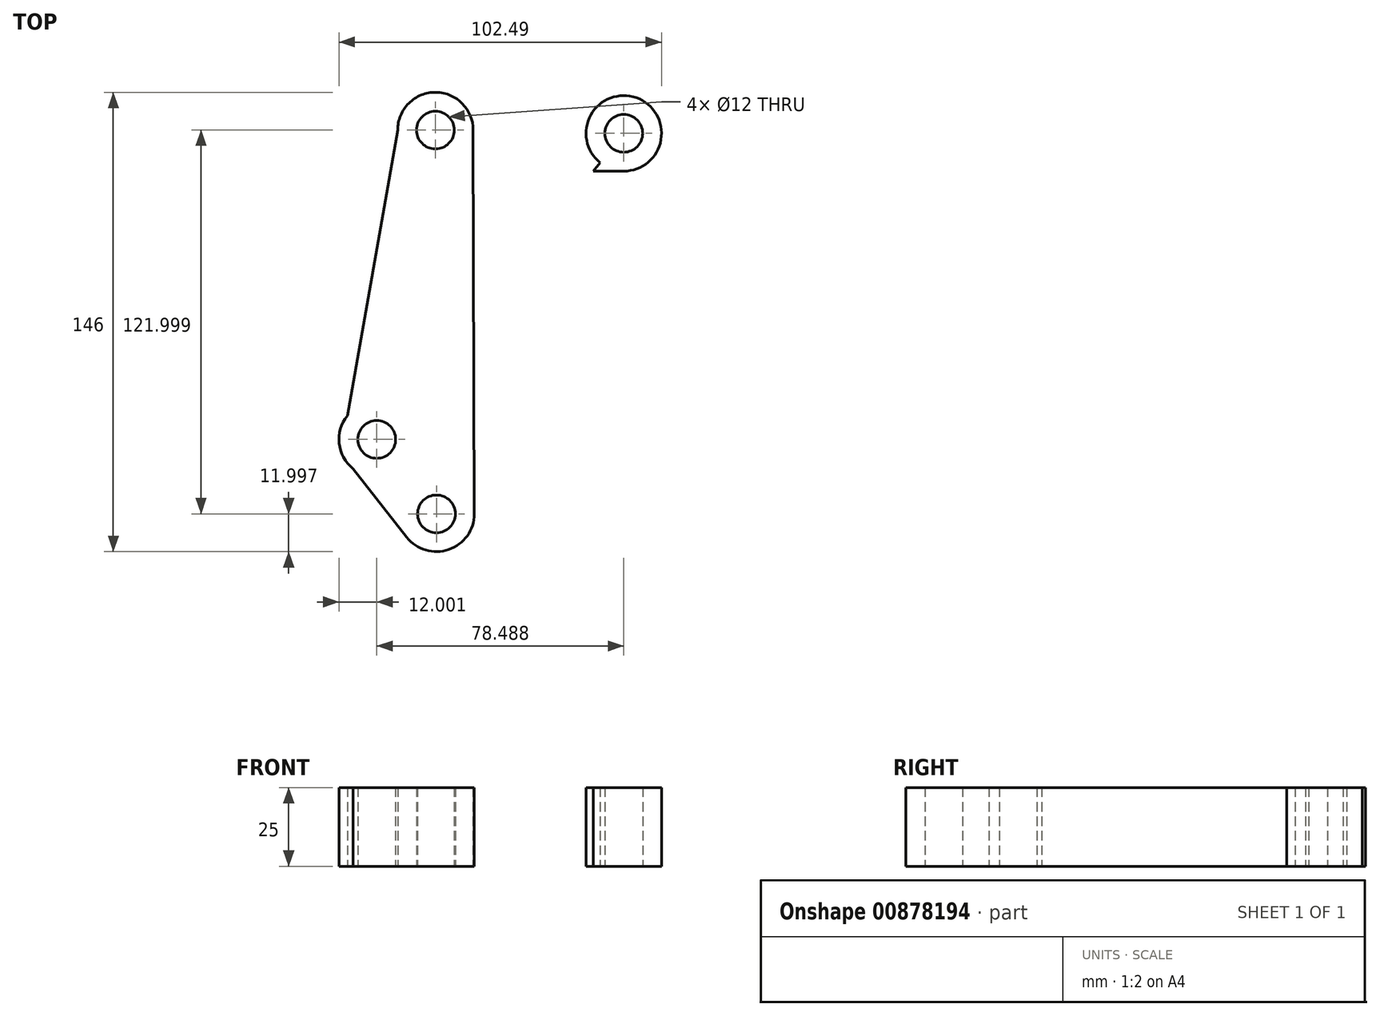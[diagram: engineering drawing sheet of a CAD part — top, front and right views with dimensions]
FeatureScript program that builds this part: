
annotation { "Feature Type Name" : "Feature", "Feature Type Description" : "" }
export const myFeature = defineFeature(function(context is Context, id is Id, definition is map)
    precondition{}
    {
        {
            var Q0;
            Q0=qCreatedBy(makeId("Top.planeOp"),FACE);
            var sketch = newSketch(context, id + "F0", { "sketchPlane" : qUnion([Q0])});
            skCircle(sketch, "E0", {"center": v(0, 0) * mm, "radius": 162 * mm, "construction": true});
            skLineSegment(sketch, "E1", {"start": v(-162, 0) * mm, "end": v(-116, 0) * mm, "construction": true});
            skLineSegment(sketch, "E2", {"start": v(-116, 0) * mm, "end": v(-70, 0) * mm, "construction": true});
            skCircle(sketch, "E3", {"center": v(0, 0) * mm, "radius": 65 * mm, "construction": true});
            skCircle(sketch, "E4", {"center": v(25.35, 59.85) * mm, "radius": 6 * mm});
            skCircle(sketch, "E5", {"center": v(-53.14, -37.43) * mm, "radius": 6 * mm});
            skLineSegment(sketch, "E6.trimOffspring", {"start": v(-22.45, 61) * mm, "end": v(-22.34, 61) * mm});
            skArc(sketch, "E7.trimOffspring", {"start": v(-22.34, 61) * mm, "mid": v(-22.34, 61.02) * mm, "end": v(-22.34, 61.04) * mm});
            skCircle(sketch, "E8", {"center": v(0, 0) * mm, "radius": 70 * mm, "construction": true});
            skLineSegment(sketch, "E9", {"start": v(25.35, 59.85) * mm, "end": v(-53.14, -37.43) * mm});
            skCircle(sketch, "E10", {"center": v(-34.5, 60.9) * mm, "radius": 6 * mm});
            skCircle(sketch, "E11", {"center": v(-34.17, -61.1) * mm, "radius": 6 * mm});
            skLineSegment(sketch, "E12", {"start": v(-34.5, 60.9) * mm, "end": v(-34.17, -61.1) * mm});
            skCircle(sketch, "E13", {"center": v(-53.14, -37.43) * mm, "radius": 12 * mm});
            skCircle(sketch, "E14", {"center": v(-34.17, -61.1) * mm, "radius": 12 * mm});
            skCircle(sketch, "E15", {"center": v(-34.5, 60.9) * mm, "radius": 12 * mm});
            skCircle(sketch, "E16", {"center": v(25.35, 59.85) * mm, "radius": 12 * mm});
            skLineSegment(sketch, "E17", {"start": v(-34.5, 60.9) * mm, "end": v(-22.5, 60.9) * mm});
            skLineSegment(sketch, "E18", {"start": v(-34.5, 60.9) * mm, "end": v(-46.5, 60.87) * mm});
            skLineSegment(sketch, "E19", {"start": v(-53.14, -37.43) * mm, "end": v(-62.48, -29.9) * mm});
            skLineSegment(sketch, "E20", {"start": v(-62.48, -29.9) * mm, "end": v(-46.5, 60.87) * mm});
            skLineSegment(sketch, "E21", {"start": v(-53.14, -37.43) * mm, "end": v(-60.67, -46.77) * mm});
            skLineSegment(sketch, "E22", {"start": v(-34.17, -61.1) * mm, "end": v(-34.17, -73.1) * mm});
            skLineSegment(sketch, "E23", {"start": v(-60.67, -46.77) * mm, "end": v(-43.6, -68.5) * mm});
            skLineSegment(sketch, "E24", {"start": v(-34.17, -61.1) * mm, "end": v(-22.17, -61.1) * mm});
            skLineSegment(sketch, "E25", {"start": v(-22.17, -61.1) * mm, "end": v(-22.5, 60.9) * mm});
            skLineSegment(sketch, "E26", {"start": v(25.35, 59.85) * mm, "end": v(25.35, 47.85) * mm});
            skLineSegment(sketch, "E27", {"start": v(25.35, 47.85) * mm, "end": v(-22.47, 47.85) * mm});
            skLineSegment(sketch, "E28", {"start": v(-34.5, 60.9) * mm, "end": v(-34.33, 72.9) * mm});
            skLineSegment(sketch, "E29", {"start": v(25.35, 59.85) * mm, "end": v(25.35, 71.85) * mm});
            skLineSegment(sketch, "E30", {"start": v(-34.33, 72.9) * mm, "end": v(25.35, 71.85) * mm});
            skSolve(sketch);
        }
        {
            var Q0;
            {var subQ0=sQuery(id+"F0.wireOp",EDGE,"E27");var subQ1=sQuery(id+"F0.wireOp",EDGE,"E9");var subQ2=makeQuery(id+"F0.imprint","INTERSECT",VERTEX,{"derivedFrom":[subQ1,subQ0]});Q0=makeQuery(id+"F0.imprint","IMPRINT",FACE,{"disambiguationData":[TD([[makeQuery(id+"F0.imprint","IMPRINT",EDGE,{"disambiguationData":[TD([[subQ2,1.0]])],"derivedFrom":subQ1}),1.0]])]});}
            var Q1;
            {var subQ0=sQuery(id+"F0.wireOp",EDGE,"E29");var subQ1=sQuery(id+"F0.wireOp",EDGE,"E4");var subQ2=makeQuery(id+"F0.imprint","INTERSECT",VERTEX,{"derivedFrom":[subQ1,subQ0]});Q1=makeQuery(id+"F0.imprint","IMPRINT",FACE,{"disambiguationData":[TD([[makeQuery(id+"F0.imprint","IMPRINT",EDGE,{"disambiguationData":[TD([[subQ2,1.0]])],"derivedFrom":subQ1}),-1.0]])]});}
            var Q2;
            {var subQ0=sQuery(id+"F0.wireOp",EDGE,"E19");var subQ1=sQuery(id+"F0.wireOp",EDGE,"E5");var subQ2=makeQuery(id+"F0.imprint","INTERSECT",VERTEX,{"derivedFrom":[subQ1,subQ0]});Q2=makeQuery(id+"F0.imprint","IMPRINT",FACE,{"disambiguationData":[TD([[makeQuery(id+"F0.imprint","IMPRINT",EDGE,{"disambiguationData":[TD([[subQ2,-1.0]])],"derivedFrom":subQ1}),-1.0]])]});}
            var Q3;
            {var subQ0=sQuery(id+"F0.wireOp",EDGE,"E25");var subQ1=sQuery(id+"F0.wireOp",EDGE,"E9");var subQ2=makeQuery(id+"F0.imprint","INTERSECT",VERTEX,{"derivedFrom":[subQ1,subQ0]});Q3=makeQuery(id+"F0.imprint","IMPRINT",FACE,{"disambiguationData":[TD([[makeQuery(id+"F0.imprint","IMPRINT",EDGE,{"disambiguationData":[TD([[subQ2,-1.0]])],"derivedFrom":subQ1}),1.0]])]});}
            var Q4;
            {var subQ0=sQuery(id+"F0.wireOp",EDGE,"E28");var subQ1=sQuery(id+"F0.wireOp",EDGE,"E10");var subQ2=makeQuery(id+"F0.imprint","INTERSECT",VERTEX,{"derivedFrom":[subQ1,subQ0]});Q4=makeQuery(id+"F0.imprint","IMPRINT",FACE,{"disambiguationData":[TD([[makeQuery(id+"F0.imprint","IMPRINT",EDGE,{"disambiguationData":[TD([[subQ2,-1.0]])],"derivedFrom":subQ1}),-1.0]])]});}
            var Q5;
            {var subQ0=sQuery(id+"F0.wireOp",EDGE,"E24");var subQ1=sQuery(id+"F0.wireOp",EDGE,"E11");var subQ2=makeQuery(id+"F0.imprint","INTERSECT",VERTEX,{"derivedFrom":[subQ1,subQ0]});Q5=makeQuery(id+"F0.imprint","IMPRINT",FACE,{"disambiguationData":[TD([[makeQuery(id+"F0.imprint","IMPRINT",EDGE,{"disambiguationData":[TD([[subQ2,1.0]])],"derivedFrom":subQ1}),-1.0]])]});}
            var Q6;
            {var subQ0=sQuery(id+"F0.wireOp",EDGE,"E9");var subQ1=sQuery(id+"F0.wireOp",EDGE,"E4");var subQ2=makeQuery(id+"F0.imprint","INTERSECT",VERTEX,{"derivedFrom":[subQ1,subQ0]});Q6=makeQuery(id+"F0.imprint","IMPRINT",FACE,{"disambiguationData":[TD([[makeQuery(id+"F0.imprint","IMPRINT",EDGE,{"disambiguationData":[TD([[subQ2,1.0]])],"derivedFrom":subQ1}),-1.0]])]});}
            var Q7;
            {var subQ0=sQuery(id+"F0.wireOp",EDGE,"E9");var subQ1=sQuery(id+"F0.wireOp",EDGE,"E4");var subQ2=makeQuery(id+"F0.imprint","INTERSECT",VERTEX,{"derivedFrom":[subQ1,subQ0]});Q7=makeQuery(id+"F0.imprint","IMPRINT",FACE,{"disambiguationData":[TD([[makeQuery(id+"F0.imprint","IMPRINT",EDGE,{"disambiguationData":[TD([[subQ2,-1.0]])],"derivedFrom":subQ1}),-1.0]])]});}
            var Q8;
            {var subQ0=sQuery(id+"F0.wireOp",EDGE,"E19");var subQ1=sQuery(id+"F0.wireOp",EDGE,"E5");var subQ2=makeQuery(id+"F0.imprint","INTERSECT",VERTEX,{"derivedFrom":[subQ1,subQ0]});Q8=makeQuery(id+"F0.imprint","IMPRINT",FACE,{"disambiguationData":[TD([[makeQuery(id+"F0.imprint","IMPRINT",EDGE,{"disambiguationData":[TD([[subQ2,1.0]])],"derivedFrom":subQ1}),-1.0]])]});}
            var Q9;
            {var subQ0=sQuery(id+"F0.wireOp",EDGE,"E9");var subQ1=sQuery(id+"F0.wireOp",EDGE,"E5");var subQ2=makeQuery(id+"F0.imprint","INTERSECT",VERTEX,{"derivedFrom":[subQ1,subQ0]});Q9=makeQuery(id+"F0.imprint","IMPRINT",FACE,{"disambiguationData":[TD([[makeQuery(id+"F0.imprint","IMPRINT",EDGE,{"disambiguationData":[TD([[subQ2,1.0]])],"derivedFrom":subQ1}),-1.0]])]});}
            var Q10;
            {var subQ0=sQuery(id+"F0.wireOp",EDGE,"E20");Q10=makeQuery(id+"F0.imprint","IMPRINT",FACE,{"disambiguationData":[TD([[makeQuery(id+"F0.imprint","IMPRINT",EDGE,{"derivedFrom":subQ0}),-1.0]])]});}
            var Q11;
            {var subQ0=sQuery(id+"F0.wireOp",EDGE,"E23");Q11=makeQuery(id+"F0.imprint","IMPRINT",FACE,{"disambiguationData":[TD([[makeQuery(id+"F0.imprint","IMPRINT",EDGE,{"derivedFrom":subQ0}),1.0]])]});}
            var Q12;
            {var subQ0=sQuery(id+"F0.wireOp",EDGE,"E28");var subQ4=sQuery(id+"F0.wireOp",EDGE,"E10");var subQ5=makeQuery(id+"F0.imprint","INTERSECT",VERTEX,{"derivedFrom":[subQ4,subQ0]});Q12=makeQuery(id+"F0.imprint","IMPRINT",FACE,{"disambiguationData":[TD([[makeQuery(id+"F0.imprint","IMPRINT",EDGE,{"disambiguationData":[TD([[subQ5,1.0]])],"derivedFrom":subQ4}),-1.0]])]});}
            var Q13;
            {var subQ0=sQuery(id+"F0.wireOp",EDGE,"E18");var subQ1=sQuery(id+"F0.wireOp",EDGE,"E10");var subQ2=makeQuery(id+"F0.imprint","INTERSECT",VERTEX,{"derivedFrom":[subQ1,subQ0]});Q13=makeQuery(id+"F0.imprint","IMPRINT",FACE,{"disambiguationData":[TD([[makeQuery(id+"F0.imprint","IMPRINT",EDGE,{"disambiguationData":[TD([[subQ2,-1.0]])],"derivedFrom":subQ1}),-1.0]])]});}
            var Q14;
            {var subQ2=sQuery(id+"F0.wireOp",EDGE,"E12");var subQ6=sQuery(id+"F0.wireOp",EDGE,"E11");var subQ7=makeQuery(id+"F0.imprint","INTERSECT",VERTEX,{"derivedFrom":[subQ6,subQ2]});Q14=makeQuery(id+"F0.imprint","IMPRINT",FACE,{"disambiguationData":[TD([[makeQuery(id+"F0.imprint","IMPRINT",EDGE,{"disambiguationData":[TD([[subQ7,1.0]])],"derivedFrom":subQ6}),-1.0]])]});}
            var Q15;
            {var subQ4=sQuery(id+"F0.wireOp",EDGE,"E12");var subQ6=sQuery(id+"F0.wireOp",EDGE,"E11");var subQ7=makeQuery(id+"F0.imprint","INTERSECT",VERTEX,{"derivedFrom":[subQ6,subQ4]});Q15=makeQuery(id+"F0.imprint","IMPRINT",FACE,{"disambiguationData":[TD([[makeQuery(id+"F0.imprint","IMPRINT",EDGE,{"disambiguationData":[TD([[subQ7,-1.0]])],"derivedFrom":subQ6}),-1.0]])]});}
            var Q16;
            {var subQ5=sQuery(id+"F0.wireOp",EDGE,"E30");Q16=makeQuery(id+"F0.imprint","IMPRINT",FACE,{"disambiguationData":[TD([[makeQuery(id+"F0.imprint","IMPRINT",EDGE,{"derivedFrom":subQ5}),-1.0]])]});}
            var Q17;
            {var subQ0=sQuery(id+"F0.wireOp",EDGE,"E25");var subQ6=sQuery(id+"F0.wireOp",EDGE,"E9");var subQ7=makeQuery(id+"F0.imprint","INTERSECT",VERTEX,{"derivedFrom":[subQ6,subQ0]});Q17=makeQuery(id+"F0.imprint","IMPRINT",FACE,{"disambiguationData":[TD([[makeQuery(id+"F0.imprint","IMPRINT",EDGE,{"disambiguationData":[TD([[subQ7,-1.0]])],"derivedFrom":subQ6}),-1.0]])]});}
            var Q18;
            {var subQ0=sQuery(id+"F0.wireOp",EDGE,"E17");var subQ1=sQuery(id+"F0.wireOp",EDGE,"E10");var subQ2=makeQuery(id+"F0.imprint","INTERSECT",VERTEX,{"derivedFrom":[subQ1,subQ0]});Q18=makeQuery(id+"F0.imprint","IMPRINT",FACE,{"disambiguationData":[TD([[makeQuery(id+"F0.imprint","IMPRINT",EDGE,{"disambiguationData":[TD([[subQ2,1.0]])],"derivedFrom":subQ1}),-1.0]])]});}
            extrude(context, id + "F1", {"entities" : qUnion([Q0, Q1, Q2, Q3, Q4, Q5, Q6, Q7, Q8, Q9, Q10, Q11, Q12, Q13, Q14, Q15, Q16, Q17, Q18]), "depth" : 25 * mm, "offsetDistance" : 25 * mm});
        }
    });
